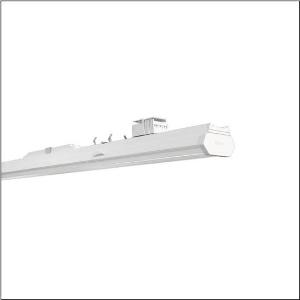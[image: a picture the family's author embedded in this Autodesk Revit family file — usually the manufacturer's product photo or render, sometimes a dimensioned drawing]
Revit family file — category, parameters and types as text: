
# Revit family: licross_r__11_protected_ho_51td11cn4exs_ee6c
name_source: partatom
category: Lighting Fixtures
units: mm (PartAtom-declared; Revit-internal decimal feet)

## family parameters
Cut with Voids When Loaded = No
Host = Face
Light Source = No
Part Type = Normal
Room Calculation Point = No
Round Connector Dimension = Use Diameter
Shared = No

## types (1)
- --- (1 x LED, 14460 lm, 77.6 W, 4000K)
    Apparent Load = 78 VA
    CIE Flux Codes = 84 94 98 99 100
    Color Rendering = 80
    Color Temperature = 4000K
    Default Elevation = 1800 mm
    Description = Licross® 11 Protected HO, luminaire insert, of sheet steel, galvanised, coil coated, white, length: 1.500mm, width: 90mm, height: 101mm, LED rated luminous flux: 14.460lm, light colour: 840, control gear: ON/OFF Multilumen, CLOi, with plug, 3-pole, with phase selection, mains connection: 220..240V, AC, 50/60Hz, start of lifetime: 78W, end of service life: 87W, halogen-free wiring, primary light control with lens, of plastic, primary optical cover: cover, of PMMA, light emission: direct distribution, primary light characteristic: symmetric, protection rating (complete): IP54, insulation class (complete): insulation class I (protective earthing), certification: CE, ENEC, VDE, UKCA, protection symbol: D if used in an environment with non-conductive dust loads with corresponding accessories, impact resistance: IK06, permissible ambient temperature for indoor applications: -35..+35°C, corresponds to IFS (International Featured Standards) requirements for safety and quality in the food industry, reducing of maximum allowable ambient temperature of 5°C with ceiling mounting, LABS conformity tested according to VDMA 24364:2018-05, packaging unit: 1 piece
    Height = 92 mm
    Lamp = 1 x LED
    Lamp Light Flux = 14460 lm
    Lamp Power = 77.6 W
    Lamp count = 1
    Length = 1500 mm
    Luminous efficacy = 186 lm/W
    Manufacturer = Siteco
    ModVariant = No
    Model = 51TD11CN4EXS
    Mounting Place = Ceiling
    Mounting Type = Pendant
    Number of Poles = 1
    OnlyDefault = Yes
    Power Factor = 1
    Product Name = Licross® 11 Protected HO
    Product group = luminaire insert
    ProductGroupID = 901
    Protection Class = Protection class I
    Protection Degree = IP 54
    RLX_Detail_Level = 1
    RLX_Emergency_Light_Flux = 0 lm
    RLX_Emergency_Type = 0
    RLX_Emergency_Type_DB = No
    RlxData = <blob elided: 22193 chars, md5=900822a9>
    Socket = socket
    Standby Power = 0 W
    System Light Flux = 14460 lm
    System Power = 78 W
    Type Comments = factory setting: luminous flux: 100 % | (A | C | E) | 181 mA
    Type Image = l_1256145.jpg
    URL = http://relux.com
    VarID = @adj_055187
    Voltage = 0 V
    Weight = 0.00 kg
    Width = 88 mm

## geometry (parser evidence)
native form markers: Blend x4, Sweep x10
no freeform markers — native parametric forms only
